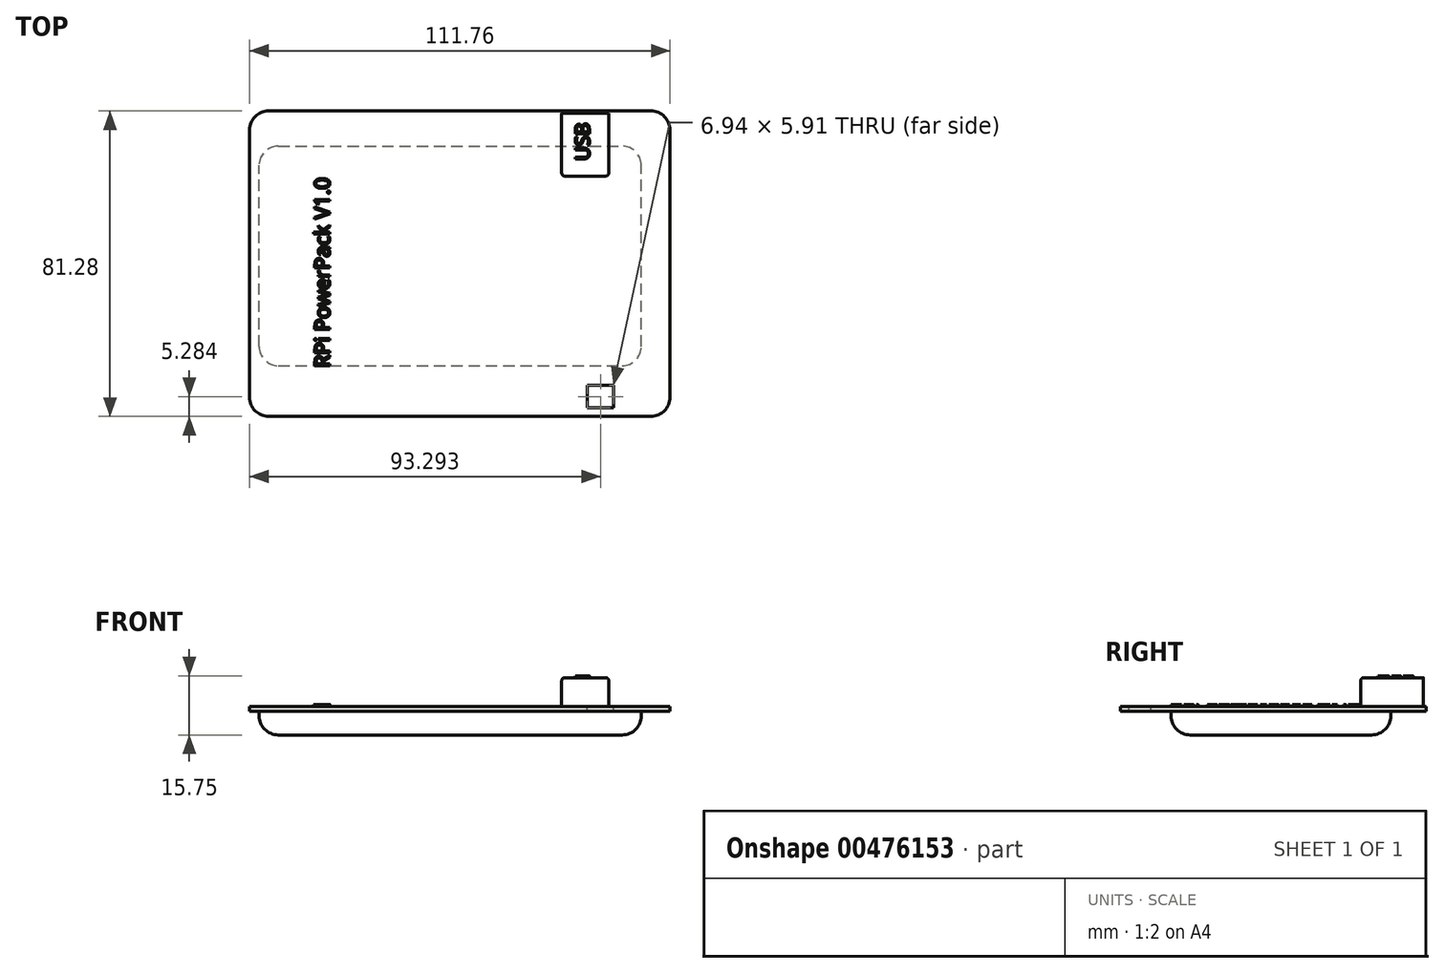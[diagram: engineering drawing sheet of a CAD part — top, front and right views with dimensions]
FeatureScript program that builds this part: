
annotation { "Feature Type Name" : "Feature", "Feature Type Description" : "" }
export const myFeature = defineFeature(function(context is Context, id is Id, definition is map)
    precondition{}
    {
        {
            var Q0;
            Q0=qCreatedBy(makeId("Top.planeOp"),FACE);
            var sketch = newSketch(context, id + "F0", { "sketchPlane" : qUnion([Q0])});
            skLineSegment(sketch, "E0.bottom", {"start": v(0, 0) * mm, "end": v(111.76, 0) * mm});
            skLineSegment(sketch, "E0.top", {"start": v(0, -81.28) * mm, "end": v(111.76, -81.28) * mm});
            skLineSegment(sketch, "E0.left", {"start": v(0, 0) * mm, "end": v(0, -81.28) * mm});
            skLineSegment(sketch, "E0.right", {"start": v(111.76, 0) * mm, "end": v(111.76, -81.28) * mm});
            skSolve(sketch);
        }
        {
            var Q0;
            Q0=makeQuery(id+"F0.imprint","IMPRINT",FACE,{"disambiguationData":[TD([[makeQuery(id+"F0.imprint","IMPRINT",EDGE,{"derivedFrom":sQuery(id+"F0.wireOp",EDGE,"E0.bottom")}),-1.0]])]});
            extrude(context, id + "F1", {"entities" : qUnion([Q0]), "depth" : 1.27 * mm});
        }
        {
            var Q0;
            Q0=makeQuery(id+"F1.opExtrude","SWEPT_EDGE",EDGE,{"disambiguationData":[OSD([sQuery(id+"F0.wireOp",EDGE,"E0.top"),sQuery(id+"F0.wireOp",EDGE,"E0.right")])]});
            var Q1;
            Q1=makeQuery(id+"F1.opExtrude","SWEPT_EDGE",EDGE,{"disambiguationData":[OSD([sQuery(id+"F0.wireOp",EDGE,"E0.top"),sQuery(id+"F0.wireOp",EDGE,"E0.left")])]});
            var Q2;
            Q2=makeQuery(id+"F1.opExtrude","SWEPT_EDGE",EDGE,{"disambiguationData":[OSD([sQuery(id+"F0.wireOp",EDGE,"E0.bottom"),sQuery(id+"F0.wireOp",EDGE,"E0.right")])]});
            var Q3;
            Q3=makeQuery(id+"F1.opExtrude","SWEPT_EDGE",EDGE,{"disambiguationData":[OSD([sQuery(id+"F0.wireOp",EDGE,"E0.bottom"),sQuery(id+"F0.wireOp",EDGE,"E0.left")])]});
            fillet(context, id + "F2", {"entities" : qUnion([Q0, Q1, Q2, Q3]), "radius" : 5.08 * mm, "tangentPropagation" : true, "allowEdgeOverflow" : false});
        }
        {
            var Q0;
            Q0=makeQuery(id+"F1.opExtrude","CAP_FACE",FACE,{"disambiguationData":[OSD([sQuery(id+"F0.wireOp",EDGE,"E0.bottom"),sQuery(id+"F0.wireOp",EDGE,"E0.top"),sQuery(id+"F0.wireOp",EDGE,"E0.left"),sQuery(id+"F0.wireOp",EDGE,"E0.right")])],"isStart":false});
            var sketch = newSketch(context, id + "F3", { "sketchPlane" : qUnion([Q0])});
            skCircle(sketch, "E1", {"center": v(104.24, -6.06) * mm, "radius": 3.3 * mm});
            skCircle(sketch, "E2", {"center": v(104.24, -75.75) * mm, "radius": 3.3 * mm});
            skCircle(sketch, "E3", {"center": v(34.94, -6.06) * mm, "radius": 3.3 * mm});
            skCircle(sketch, "E4", {"center": v(34.94, -75.75) * mm, "radius": 3.3 * mm});
            skSolve(sketch);
        }
        {
            var Q0;
            Q0=makeQuery(id+"F1.opExtrude","CAP_FACE",FACE,{"disambiguationData":[OSD([sQuery(id+"F0.wireOp",EDGE,"E0.bottom"),sQuery(id+"F0.wireOp",EDGE,"E0.top"),sQuery(id+"F0.wireOp",EDGE,"E0.left"),sQuery(id+"F0.wireOp",EDGE,"E0.right")])],"isStart":true});
            var sketch = newSketch(context, id + "F4", { "sketchPlane" : qUnion([Q0])});
            skLineSegment(sketch, "E5.bottom", {"start": v(2.54, 67.77) * mm, "end": v(104.14, 67.77) * mm});
            skLineSegment(sketch, "E5.top", {"start": v(2.54, 9.35) * mm, "end": v(104.14, 9.35) * mm});
            skLineSegment(sketch, "E5.left", {"start": v(2.54, 67.77) * mm, "end": v(2.54, 9.35) * mm});
            skLineSegment(sketch, "E5.right", {"start": v(104.14, 67.77) * mm, "end": v(104.14, 9.35) * mm});
            skSolve(sketch);
        }
        {
            var Q0;
            Q0=makeQuery(id+"F4.imprint","IMPRINT",FACE,{"disambiguationData":[TD([[makeQuery(id+"F4.imprint","IMPRINT",EDGE,{"derivedFrom":sQuery(id+"F4.wireOp",EDGE,"E5.bottom")}),-1.0]])]});
            extrude(context, id + "F5", {"entities" : qUnion([Q0]), "operationType" : NewBodyOperationType.ADD, "depth" : 6.35 * mm});
        }
        {
            var Q0;
            Q0=makeQuery(id+"F5.opExtrude","CAP_EDGE",EDGE,{"disambiguationData":[OSD([sQuery(id+"F4.wireOp",EDGE,"E5.top")])],"isStart":false});
            var Q1;
            Q1=makeQuery(id+"F5.opExtrude","CAP_EDGE",EDGE,{"disambiguationData":[OSD([sQuery(id+"F4.wireOp",EDGE,"E5.left")])],"isStart":false});
            var Q2;
            Q2=makeQuery(id+"F5.opExtrude","CAP_EDGE",EDGE,{"disambiguationData":[OSD([sQuery(id+"F4.wireOp",EDGE,"E5.bottom")])],"isStart":false});
            var Q3;
            Q3=makeQuery(id+"F5.opExtrude","CAP_EDGE",EDGE,{"disambiguationData":[OSD([sQuery(id+"F4.wireOp",EDGE,"E5.right")])],"isStart":false});
            fillet(context, id + "F6", {"entities" : qUnion([Q0, Q1, Q2, Q3]), "radius" : 5.08 * mm, "tangentPropagation" : true, "allowEdgeOverflow" : false});
        }
        {
            var Q0;
            Q0=makeQuery(id+"F6.opFillet","BLEND_EDGE",EDGE,{"blendedFrom":[makeQuery(id+"F5.opExtrude","CAP_EDGE",EDGE,{"disambiguationData":[OSD([sQuery(id+"F4.wireOp",EDGE,"E5.bottom")])],"isStart":false}),makeQuery(id+"F5.opExtrude","CAP_EDGE",EDGE,{"disambiguationData":[OSD([sQuery(id+"F4.wireOp",EDGE,"E5.left")])],"isStart":false})],"blendedInto":[]});
            var Q1;
            Q1=makeQuery(id+"F6.opFillet","BLEND_EDGE",EDGE,{"blendedFrom":[makeQuery(id+"F5.opExtrude","CAP_EDGE",EDGE,{"disambiguationData":[OSD([sQuery(id+"F4.wireOp",EDGE,"E5.bottom")])],"isStart":false}),makeQuery(id+"F5.opExtrude","CAP_EDGE",EDGE,{"disambiguationData":[OSD([sQuery(id+"F4.wireOp",EDGE,"E5.right")])],"isStart":false})],"blendedInto":[]});
            var Q2;
            Q2=makeQuery(id+"F6.opFillet","BLEND_EDGE",EDGE,{"blendedFrom":[makeQuery(id+"F5.opExtrude","CAP_EDGE",EDGE,{"disambiguationData":[OSD([sQuery(id+"F4.wireOp",EDGE,"E5.top")])],"isStart":false}),makeQuery(id+"F5.opExtrude","CAP_EDGE",EDGE,{"disambiguationData":[OSD([sQuery(id+"F4.wireOp",EDGE,"E5.right")])],"isStart":false})],"blendedInto":[]});
            var Q3;
            Q3=makeQuery(id+"F6.opFillet","BLEND_EDGE",EDGE,{"blendedFrom":[makeQuery(id+"F5.opExtrude","CAP_EDGE",EDGE,{"disambiguationData":[OSD([sQuery(id+"F4.wireOp",EDGE,"E5.top")])],"isStart":false}),makeQuery(id+"F5.opExtrude","CAP_EDGE",EDGE,{"disambiguationData":[OSD([sQuery(id+"F4.wireOp",EDGE,"E5.left")])],"isStart":false})],"blendedInto":[]});
            fillet(context, id + "F7", {"entities" : qUnion([Q0, Q1, Q2, Q3]), "radius" : 5.08 * mm, "tangentPropagation" : true, "allowEdgeOverflow" : false});
        }
        {
            var Q0;
            Q0=makeQuery(id+"F1.opExtrude","CAP_FACE",FACE,{"disambiguationData":[OSD([sQuery(id+"F0.wireOp",EDGE,"E0.bottom"),sQuery(id+"F0.wireOp",EDGE,"E0.top"),sQuery(id+"F0.wireOp",EDGE,"E0.left"),sQuery(id+"F0.wireOp",EDGE,"E0.right")])],"isStart":false});
            var sketch = newSketch(context, id + "F8", { "sketchPlane" : qUnion([Q0])});
            skLineSegment(sketch, "E6.bottom", {"start": v(96.76, -78.95) * mm, "end": v(89.82, -78.95) * mm});
            skLineSegment(sketch, "E6.top", {"start": v(96.76, -73.04) * mm, "end": v(89.82, -73.04) * mm});
            skLineSegment(sketch, "E6.left", {"start": v(96.76, -78.95) * mm, "end": v(96.76, -73.04) * mm});
            skLineSegment(sketch, "E6.right", {"start": v(89.82, -78.95) * mm, "end": v(89.82, -73.04) * mm});
            skSolve(sketch);
        }
        {
            var Q0;
            Q0=makeQuery(id+"F8.imprint","IMPRINT",FACE,{"disambiguationData":[TD([[makeQuery(id+"F8.imprint","IMPRINT",EDGE,{"derivedFrom":sQuery(id+"F8.wireOp",EDGE,"E6.bottom")}),-1.0]])]});
            extrude(context, id + "F9", {"entities" : qUnion([Q0]), "operationType" : NewBodyOperationType.REMOVE, "oppositeDirection" : true, "depth" : 5.08 * mm});
        }
        {
            var Q0;
            Q0=makeQuery(id+"F8.imprint","IMPRINT",FACE,{"disambiguationData":[TD([[makeQuery(id+"F8.imprint","IMPRINT",EDGE,{"derivedFrom":sQuery(id+"F8.wireOp",EDGE,"E6.bottom")}),1.0]])]});
            var sketch = newSketch(context, id + "F10", { "sketchPlane" : qUnion([Q0])});
            skLineSegment(sketch, "E7.bottom", {"start": v(82.97, -17.32) * mm, "end": v(95.45, -17.32) * mm});
            skLineSegment(sketch, "E7.top", {"start": v(82.97, -0.66) * mm, "end": v(95.45, -0.66) * mm});
            skLineSegment(sketch, "E7.left", {"start": v(82.97, -17.32) * mm, "end": v(82.97, -0.66) * mm});
            skLineSegment(sketch, "E7.right", {"start": v(95.45, -17.32) * mm, "end": v(95.45, -0.66) * mm});
            skSolve(sketch);
        }
        {
            var Q0;
            Q0=makeQuery(id+"F10.imprint","IMPRINT",FACE,{"disambiguationData":[TD([[makeQuery(id+"F10.imprint","IMPRINT",EDGE,{"derivedFrom":sQuery(id+"F10.wireOp",EDGE,"E7.bottom")}),1.0]])]});
            extrude(context, id + "F11", {"entities" : qUnion([Q0]), "operationType" : NewBodyOperationType.ADD, "depth" : 7.62 * mm});
        }
        {
            var Q0;
            Q0=makeQuery(id+"F8.imprint","IMPRINT",FACE,{"disambiguationData":[TD([[makeQuery(id+"F8.imprint","IMPRINT",EDGE,{"derivedFrom":sQuery(id+"F8.wireOp",EDGE,"E6.bottom")}),1.0]])]});
            var sketch = newSketch(context, id + "F12", { "sketchPlane" : qUnion([Q0])});
            skText(sketch, "E8", { "text": "RPi PowerPack V1.0", "fontName": "OpenSans-Regular.ttf"});
            const initialGuessF12  = {"E8": [0.02128, -0.0683, 0, 1, 0.004]};
            skSetInitialGuess(sketch, initialGuessF12);
            skSolve(sketch);
        }
        {
            var Q0;
            Q0 = qSketchRegion(id + "F12", true);
            extrude(context, id + "F13", {"entities" : qUnion([Q0]), "operationType" : NewBodyOperationType.ADD, "depth" : 0.5 * mm});
        }
        {
            var Q0;
            Q0=makeQuery(id+"F11.opExtrude","CAP_EDGE",EDGE,{"disambiguationData":[OSD([sQuery(id+"F10.wireOp",EDGE,"E7.left")])],"isStart":false});
            var Q1;
            Q1=makeQuery(id+"F11.opExtrude","CAP_EDGE",EDGE,{"disambiguationData":[OSD([sQuery(id+"F10.wireOp",EDGE,"E7.right")])],"isStart":false});
            var Q2;
            Q2=makeQuery(id+"F11.opExtrude","CAP_EDGE",EDGE,{"disambiguationData":[OSD([sQuery(id+"F10.wireOp",EDGE,"E7.bottom")])],"isStart":false});
            var Q3;
            Q3=makeQuery(id+"F11.opExtrude","SWEPT_EDGE",EDGE,{"disambiguationData":[OSD([sQuery(id+"F10.wireOp",EDGE,"E7.bottom"),sQuery(id+"F10.wireOp",EDGE,"E7.right")])]});
            var Q4;
            Q4=makeQuery(id+"F11.opExtrude","SWEPT_EDGE",EDGE,{"disambiguationData":[OSD([sQuery(id+"F10.wireOp",EDGE,"E7.bottom"),sQuery(id+"F10.wireOp",EDGE,"E7.left")])]});
            fillet(context, id + "F14", {"entities" : qUnion([Q0, Q1, Q2, Q3, Q4]), "radius" : 0.76 * mm, "tangentPropagation" : true, "allowEdgeOverflow" : false});
        }
        {
            var Q0;
            Q0=makeQuery(id+"F11.opExtrude","CAP_FACE",FACE,{"disambiguationData":[OSD([sQuery(id+"F10.wireOp",EDGE,"E7.bottom"),sQuery(id+"F10.wireOp",EDGE,"E7.top"),sQuery(id+"F10.wireOp",EDGE,"E7.left"),sQuery(id+"F10.wireOp",EDGE,"E7.right")])],"isStart":false});
            var sketch = newSketch(context, id + "F15", { "sketchPlane" : qUnion([Q0])});
            skText(sketch, "E9", { "text": "USB", "fontName": "OpenSans-Regular.ttf"});
            const initialGuessF15  = {"E9": [0.09034, -0.01323, 0, 1, 0.00378]};
            skSetInitialGuess(sketch, initialGuessF15);
            skSolve(sketch);
        }
        {
            var Q0;
            Q0 = qSketchRegion(id + "F15", true);
            extrude(context, id + "F16", {"entities" : qUnion([Q0]), "operationType" : NewBodyOperationType.ADD, "depth" : 0.5 * mm});
        }
    });
